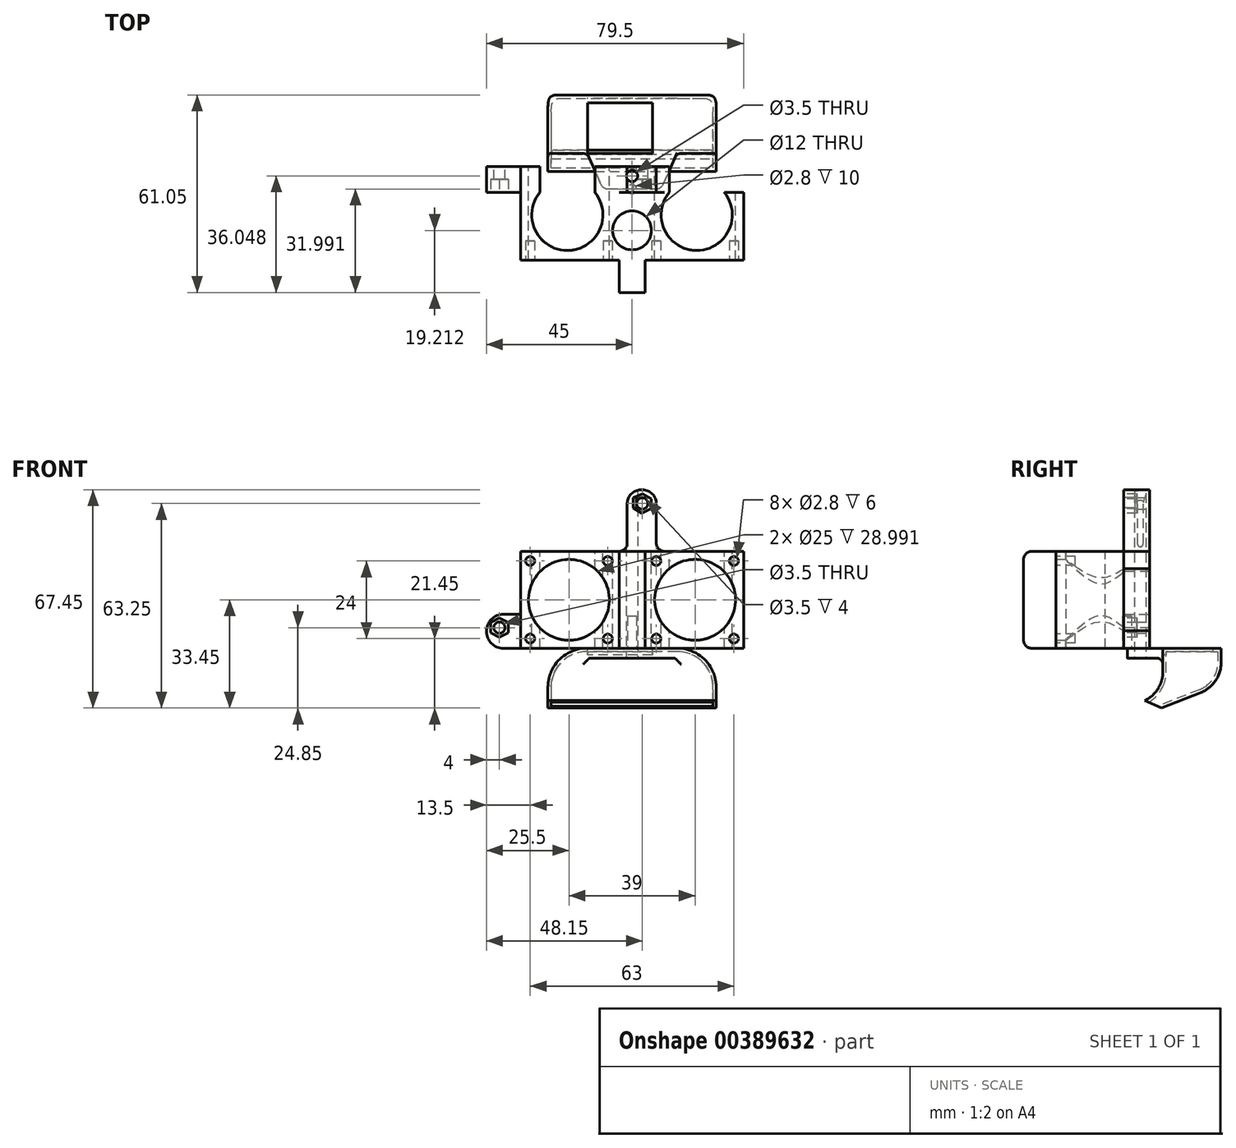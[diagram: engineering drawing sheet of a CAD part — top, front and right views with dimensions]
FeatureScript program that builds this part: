
annotation { "Feature Type Name" : "Feature", "Feature Type Description" : "" }
export const myFeature = defineFeature(function(context is Context, id is Id, definition is map)
    precondition{}
    {
        {
            var Q0;
            Q0=qCreatedBy(makeId("Front.planeOp"),FACE);
            var sketch = newSketch(context, id + "F0", { "sketchPlane" : qUnion([Q0])});
            skLineSegment(sketch, "E0.bottom", {"start": v(-34.5, 15) * mm, "end": v(-4.5, 15) * mm});
            skLineSegment(sketch, "E0.top", {"start": v(-34.5, -15) * mm, "end": v(-4.5, -15) * mm});
            skLineSegment(sketch, "E0.left", {"start": v(-34.5, 15) * mm, "end": v(-34.5, -15) * mm});
            skLineSegment(sketch, "E0.right", {"start": v(-4.5, 15) * mm, "end": v(-4.5, -15) * mm});
            skLineSegment(sketch, "E1.bottom", {"start": v(-31.5, 12) * mm, "end": v(-7.5, 12) * mm, "construction": true});
            skLineSegment(sketch, "E1.top", {"start": v(-31.5, -12) * mm, "end": v(-7.5, -12) * mm, "construction": true});
            skLineSegment(sketch, "E1.left", {"start": v(-31.5, 12) * mm, "end": v(-31.5, -12) * mm, "construction": true});
            skLineSegment(sketch, "E1.right", {"start": v(-7.5, 12) * mm, "end": v(-7.5, -12) * mm, "construction": true});
            skCircle(sketch, "E2", {"center": v(-31.5, 12) * mm, "radius": 1.4 * mm, "construction": true});
            skCircle(sketch, "E3", {"center": v(-7.5, 12) * mm, "radius": 1.4 * mm, "construction": true});
            skCircle(sketch, "E4", {"center": v(-7.5, -12) * mm, "radius": 1.4 * mm, "construction": true});
            skCircle(sketch, "E5", {"center": v(-31.5, -12) * mm, "radius": 1.4 * mm, "construction": true});
            skPoint(sketch, "E6", {"position": v(-19.5, 0) * mm});
            skPoint(sketch, "E6.positionSnap0", {"position": v(-7.5, 0) * mm});
            skPoint(sketch, "E6.positionSnap1", {"position": v(-19.5, -12) * mm});
            skCircle(sketch, "E7", {"center": v(-19.5, 0) * mm, "radius": 12.5 * mm});
            skLineSegment(sketch, "E8.bottom", {"start": v(-4.5, 15) * mm, "end": v(0, 15) * mm});
            skLineSegment(sketch, "E8.top", {"start": v(-4.5, -15) * mm, "end": v(0, -15) * mm});
            skLineSegment(sketch, "E8.right", {"start": v(0, 15) * mm, "end": v(0, -15) * mm});
            skSolve(sketch);
        }
        {
            var Q0;
            Q0=qSketchRegion(id+"F0",true);
            extrude(context, id + "F1", {"entities" : qUnion([Q0]), "depth" : 28 * mm});
        }
        {
            var Q0;
            Q0=makeQuery(id+"F1.opExtrude","SWEPT_FACE",FACE,{"disambiguationData":[OSD([sQuery(id+"F0.wireOp",EDGE,"E0.bottom")])]});
            var sketch = newSketch(context, id + "F2", { "sketchPlane" : qUnion([Q0])});
            skPoint(sketch, "E9.positionSnap0", {"position": v(-20, -28) * mm});
            skPoint(sketch, "E9.positionSnap1", {"position": v(-34.5, -14) * mm});
            skCircle(sketch, "E10", {"center": v(-20, -14) * mm, "radius": 11 * mm});
            skSolve(sketch);
        }
        {
            var Q0;
            Q0=qSketchRegion(id+"F2",true);
            extrude(context, id + "F3", {"entities" : qUnion([Q0]), "operationType" : NewBodyOperationType.REMOVE, "endBound" : BoundingType.THROUGH_ALL, "oppositeDirection" : true, "depth" : 25 * mm});
        }
        {
            var Q0;
            Q0=makeQuery(id+"F1.opExtrude","SWEPT_FACE",FACE,{"disambiguationData":[OSD([sQuery(id+"F0.wireOp",EDGE,"E0.bottom")])]});
            var sketch = newSketch(context, id + "F4", { "sketchPlane" : qUnion([Q0])});
            skLineSegment(sketch, "E11.bottom", {"start": v(-34.5, 0) * mm, "end": v(0, 0) * mm});
            skLineSegment(sketch, "E11.top", {"start": v(-34.5, -7) * mm, "end": v(0, -7) * mm});
            skLineSegment(sketch, "E11.left", {"start": v(-34.5, 0) * mm, "end": v(-34.5, -7) * mm});
            skLineSegment(sketch, "E11.right", {"start": v(0, 0) * mm, "end": v(0, -7) * mm});
            skSolve(sketch);
        }
        {
            var Q0;
            Q0=qSketchRegion(id+"F4",true);
            extrude(context, id + "F5", {"entities" : qUnion([Q0]), "operationType" : NewBodyOperationType.REMOVE, "endBound" : BoundingType.THROUGH_ALL, "oppositeDirection" : true, "depth" : 25 * mm});
        }
        {
            var Q0;
            Q0=makeQuery(id+"F1.opExtrude","CAP_FACE",FACE,{"disambiguationData":[OSD([sQuery(id+"F0.wireOp",EDGE,"E0.bottom"),sQuery(id+"F0.wireOp",EDGE,"E0.top"),sQuery(id+"F0.wireOp",EDGE,"E0.left"),sQuery(id+"F0.wireOp",EDGE,"E0.right"),sQuery(id+"F0.wireOp",EDGE,"E7")])],"isStart":false});
            var sketch = newSketch(context, id + "F6", { "sketchPlane" : qUnion([Q0])});
            skCircle(sketch, "E12.0", {"center": v(-31.5, 12) * mm, "radius": 1.4 * mm});
            skCircle(sketch, "E13.0", {"center": v(-7.5, 12) * mm, "radius": 1.4 * mm});
            skCircle(sketch, "E14.0", {"center": v(-7.5, -12) * mm, "radius": 1.4 * mm});
            skCircle(sketch, "E15.0", {"center": v(-31.5, -12) * mm, "radius": 1.4 * mm});
            skSolve(sketch);
        }
        {
            var Q0;
            Q0=qSketchRegion(id+"F6",true);
            extrude(context, id + "F7", {"entities" : qUnion([Q0]), "operationType" : NewBodyOperationType.REMOVE, "oppositeDirection" : true, "depth" : 6 * mm});
        }
        {
            var Q0;
            Q0=makeQuery(id+"F1.opExtrude","SWEPT_BODY",BODY,{"disambiguationData":[OSD([sQuery(id+"F0.wireOp",EDGE,"E0.bottom"),sQuery(id+"F0.wireOp",EDGE,"E0.top"),sQuery(id+"F0.wireOp",EDGE,"E0.left"),sQuery(id+"F0.wireOp",EDGE,"E0.right"),sQuery(id+"F0.wireOp",EDGE,"E7")])]});
            var Q1;
            Q1=qCreatedBy(makeId("Right.planeOp"),FACE);
            mirror(context, id + "F8", {"entities" : qUnion([Q0]), "mirrorPlane" : qUnion([Q1])});
        }
        {
            var Q0;
            Q0=makeQuery(id+"F1.opExtrude","SWEPT_BODY",BODY,{"disambiguationData":[OSD([sQuery(id+"F0.wireOp",EDGE,"E0.bottom"),sQuery(id+"F0.wireOp",EDGE,"E0.top"),sQuery(id+"F0.wireOp",EDGE,"E0.left"),sQuery(id+"F0.wireOp",EDGE,"E7"),sQuery(id+"F0.wireOp",EDGE,"E8.bottom"),sQuery(id+"F0.wireOp",EDGE,"E8.top"),sQuery(id+"F0.wireOp",EDGE,"E8.right")])]});
            var Q1;
            Q1=makeQuery(id+"F8.opPattern","COPY",BODY,{"derivedFrom":makeQuery(id+"F1.opExtrude","SWEPT_BODY",BODY,{"disambiguationData":[OSD([sQuery(id+"F0.wireOp",EDGE,"E0.bottom"),sQuery(id+"F0.wireOp",EDGE,"E0.top"),sQuery(id+"F0.wireOp",EDGE,"E0.left"),sQuery(id+"F0.wireOp",EDGE,"E7"),sQuery(id+"F0.wireOp",EDGE,"E8.bottom"),sQuery(id+"F0.wireOp",EDGE,"E8.top"),sQuery(id+"F0.wireOp",EDGE,"E8.right")])]}),"instanceName":"1"});
            booleanBodies(context, id + "F9", {"operationType" : BooleanOperationType.UNION, "tools" : qUnion([Q0, Q1])});
        }
        {
            var Q0;
            {var subQ0=makeQuery(id+"F5.boolean.opBoolean","COPY",FACE,{"disambiguationData":[TD([makeQuery(id+"F1.opExtrude","SWEPT_FACE",FACE,{"disambiguationData":[OSD([sQuery(id+"F0.wireOp",EDGE,"E8.right")])]})])],"derivedFrom":makeQuery(id+"F5.opExtrude","SWEPT_FACE",FACE,{"disambiguationData":[OSD([sQuery(id+"F4.wireOp",EDGE,"E11.top")])]})});Q0=makeQuery(id+"F9.opBoolean","MERGE",FACE,{"derivedFrom":[subQ0,makeQuery(id+"F8.opPattern","COPY",FACE,{"derivedFrom":subQ0,"instanceName":"1"})]});}
            var sketch = newSketch(context, id + "F10", { "sketchPlane" : qUnion([Q0])});
            skLineSegment(sketch, "E16.bottom", {"start": v(-7.5, 15) * mm, "end": v(1.5, 15) * mm});
            skLineSegment(sketch, "E16.top", {"start": v(-7.5, 34) * mm, "end": v(1.5, 34) * mm});
            skLineSegment(sketch, "E16.left", {"start": v(-7.5, 15) * mm, "end": v(-7.5, 34) * mm});
            skLineSegment(sketch, "E16.right", {"start": v(1.5, 15) * mm, "end": v(1.5, 34) * mm});
            skPoint(sketch, "E17.orphan", {"position": v(0, 34) * mm});
            skLineSegment(sketch, "E18.0.0", {"start": v(11.5, -9.61) * mm, "end": v(11.5, -15) * mm});
            skArc(sketch, "E18.0.1", {"start": v(11.5, -9.61) * mm, "mid": v(7, 0) * mm, "end": v(11.5, 9.61) * mm});
            skLineSegment(sketch, "E18.0.2", {"start": v(11.5, 15) * mm, "end": v(11.5, 9.61) * mm});
            skLineSegment(sketch, "E18.0.3", {"start": v(11.5, 15) * mm, "end": v(-11.5, 15) * mm});
            skLineSegment(sketch, "E18.0.4", {"start": v(-11.5, 15) * mm, "end": v(-11.5, 9.61) * mm});
            skArc(sketch, "E18.0.5", {"start": v(-11.5, 9.61) * mm, "mid": v(-7, 0) * mm, "end": v(-11.5, -9.61) * mm});
            skLineSegment(sketch, "E18.0.6", {"start": v(-11.5, -9.61) * mm, "end": v(-11.5, -15) * mm});
            skLineSegment(sketch, "E18.0.7", {"start": v(-11.5, -15) * mm, "end": v(11.5, -15) * mm});
            skLineSegment(sketch, "E19.0.0", {"start": v(34.5, -15) * mm, "end": v(34.5, 15) * mm});
            skLineSegment(sketch, "E19.0.1", {"start": v(34.5, 15) * mm, "end": v(28.5, 15) * mm});
            skLineSegment(sketch, "E19.0.2", {"start": v(28.5, 15) * mm, "end": v(28.5, 8.68) * mm});
            skArc(sketch, "E19.0.3", {"start": v(28.5, 8.68) * mm, "mid": v(32, 0) * mm, "end": v(28.5, -8.68) * mm});
            skLineSegment(sketch, "E19.0.4", {"start": v(28.5, -8.68) * mm, "end": v(28.5, -15) * mm});
            skLineSegment(sketch, "E19.0.5", {"start": v(28.5, -15) * mm, "end": v(34.5, -15) * mm});
            skSolve(sketch);
        }
        {
            var Q0;
            Q0=qSketchRegion(id+"F10",true);
            extrude(context, id + "F11", {"entities" : qUnion([Q0]), "operationType" : NewBodyOperationType.ADD, "depth" : 8 * mm});
        }
        {
            var Q0;
            Q0=makeQuery(id+"F11.opExtrude","SWEPT_EDGE",EDGE,{"disambiguationData":[OSD([sQuery(id+"F10.wireOp",EDGE,"E16.top"),sQuery(id+"F10.wireOp",EDGE,"E16.right")])]});
            var Q1;
            Q1=makeQuery(id+"F11.opExtrude","SWEPT_EDGE",EDGE,{"disambiguationData":[OSD([sQuery(id+"F10.wireOp",EDGE,"E16.top"),sQuery(id+"F10.wireOp",EDGE,"E16.left")])]});
            fillet(context, id + "F12", {"entities" : qUnion([Q0, Q1]), "radius" : 4.25 * mm, "tangentPropagation" : true, "allowEdgeOverflow" : false});
        }
        {
            var Q0;
            Q0=makeQuery(id+"F11.opExtrude","CAP_FACE",FACE,{"disambiguationData":[OSD([sQuery(id+"F10.wireOp",EDGE,"E19.0.0"),sQuery(id+"F10.wireOp",EDGE,"E19.0.1"),sQuery(id+"F10.wireOp",EDGE,"E19.0.2"),sQuery(id+"F10.wireOp",EDGE,"E19.0.3"),sQuery(id+"F10.wireOp",EDGE,"E19.0.4"),sQuery(id+"F10.wireOp",EDGE,"E19.0.5")])],"isStart":false});
            var sketch = newSketch(context, id + "F13", { "sketchPlane" : qUnion([Q0])});
            skLineSegment(sketch, "E20.bottom", {"start": v(34.5, -4.5) * mm, "end": v(45, -4.5) * mm});
            skLineSegment(sketch, "E20.top", {"start": v(34.5, -15) * mm, "end": v(45, -15) * mm});
            skLineSegment(sketch, "E20.left", {"start": v(34.5, -4.5) * mm, "end": v(34.5, -15) * mm});
            skLineSegment(sketch, "E20.right", {"start": v(45, -4.5) * mm, "end": v(45, -15) * mm});
            skSolve(sketch);
        }
        {
            var Q0;
            Q0=qSketchRegion(id+"F13",true);
            extrude(context, id + "F14", {"entities" : qUnion([Q0]), "operationType" : NewBodyOperationType.ADD, "oppositeDirection" : true, "depth" : 8 * mm});
        }
        {
            var Q0;
            Q0=makeQuery(id+"F14.boolean.opBoolean","MERGE",FACE,{"derivedFrom":[makeQuery(id+"F11.opExtrude","CAP_FACE",FACE,{"disambiguationData":[OSD([sQuery(id+"F10.wireOp",EDGE,"d3302207-0b7b-4ae5-a757-db3abba19617.0.0"),sQuery(id+"F10.wireOp",EDGE,"d3302207-0b7b-4ae5-a757-db3abba19617.0.1"),sQuery(id+"F10.wireOp",EDGE,"d3302207-0b7b-4ae5-a757-db3abba19617.0.2"),sQuery(id+"F10.wireOp",EDGE,"d3302207-0b7b-4ae5-a757-db3abba19617.0.3"),sQuery(id+"F10.wireOp",EDGE,"d3302207-0b7b-4ae5-a757-db3abba19617.0.4"),sQuery(id+"F10.wireOp",EDGE,"d3302207-0b7b-4ae5-a757-db3abba19617.0.5")])],"isStart":false}),makeQuery(id+"F14.opExtrude","CAP_FACE",FACE,{"disambiguationData":[OSD([sQuery(id+"F13.wireOp",EDGE,"E20.bottom"),sQuery(id+"F13.wireOp",EDGE,"E20.top"),sQuery(id+"F13.wireOp",EDGE,"E20.left"),sQuery(id+"F13.wireOp",EDGE,"E20.right")])],"isStart":true})]});
            var sketch = newSketch(context, id + "F15", { "sketchPlane" : qUnion([Q0])});
            skCircle(sketch, "E21", {"center": v(41, -8.6) * mm, "radius": 1.75 * mm});
            skCircle(sketch, "E22", {"center": v(-3.15, 29.8) * mm, "radius": 1.75 * mm});
            skSolve(sketch);
        }
        {
            var Q0;
            Q0=qSketchRegion(id+"F15",true);
            extrude(context, id + "F16", {"entities" : qUnion([Q0]), "operationType" : NewBodyOperationType.REMOVE, "endBound" : BoundingType.THROUGH_ALL, "oppositeDirection" : true, "depth" : 25 * mm});
        }
        {
            var Q0;
            {var subQ0=sQuery(id+"F10.wireOp",EDGE,"67f7da67-8d9d-40b1-a9e6-b95f429b4137.0.0");var subQ1=makeQuery(id+"F1.opExtrude","SWEPT_FACE",FACE,{"disambiguationData":[OSD([sQuery(id+"F0.wireOp",EDGE,"E0.bottom"),sQuery(id+"F0.wireOp",EDGE,"E8.bottom")])]});var subQ3=sQuery(id+"F10.wireOp",EDGE,"E16.bottom");var subQ4=subQ1;Q0=makeQuery(id+"F11.boolean.opBoolean","MERGE",FACE,{"derivedFrom":[makeQuery(id+"F9.opBoolean","MERGE",FACE,{"derivedFrom":[subQ4,makeQuery(id+"F8.opPattern","COPY",FACE,{"derivedFrom":subQ4,"instanceName":"1"})]}),makeQuery(id+"F11.opExtrude","SWEPT_FACE",FACE,{"disambiguationData":[OSD([subQ0]),TDD([makeQuery(id+"F10.imprint","IMPRINT",EDGE,{"disambiguationData":[TD([[makeQuery(id+"F10.imprint","INTERSECT",VERTEX,{"derivedFrom":[subQ0,subQ3,sQuery(id+"F10.wireOp",EDGE,"E16.right")]}),1.0]])],"derivedFrom":subQ0})])]}),makeQuery(id+"F11.opExtrude","SWEPT_FACE",FACE,{"disambiguationData":[OSD([subQ0]),TDD([makeQuery(id+"F10.imprint","IMPRINT",EDGE,{"disambiguationData":[TD([[makeQuery(id+"F10.imprint","INTERSECT",VERTEX,{"derivedFrom":[subQ0,subQ3,sQuery(id+"F10.wireOp",EDGE,"E16.left")]}),-1.0]])],"derivedFrom":subQ0})])]}),makeQuery(id+"F11.opExtrude","SWEPT_FACE",FACE,{"disambiguationData":[OSD([sQuery(id+"F10.wireOp",EDGE,"d3302207-0b7b-4ae5-a757-db3abba19617.0.1")])]})]});}
            var sketch = newSketch(context, id + "F17", { "sketchPlane" : qUnion([Q0])});
            skCircle(sketch, "E23", {"center": v(0, -18.79) * mm, "radius": 6 * mm});
            skSolve(sketch);
        }
        {
            var Q0;
            Q0=qSketchRegion(id+"F17",true);
            extrude(context, id + "F18", {"entities" : qUnion([Q0]), "operationType" : NewBodyOperationType.REMOVE, "endBound" : BoundingType.THROUGH_ALL, "oppositeDirection" : true, "depth" : 25 * mm});
        }
        {
            var Q0;
            {var subQ0=makeQuery(id+"F1.opExtrude","CAP_FACE",FACE,{"disambiguationData":[OSD([sQuery(id+"F0.wireOp",EDGE,"E0.bottom"),sQuery(id+"F0.wireOp",EDGE,"E0.top"),sQuery(id+"F0.wireOp",EDGE,"E0.left"),sQuery(id+"F0.wireOp",EDGE,"E7"),sQuery(id+"F0.wireOp",EDGE,"E8.bottom"),sQuery(id+"F0.wireOp",EDGE,"E8.top"),sQuery(id+"F0.wireOp",EDGE,"E8.right")])],"isStart":false});Q0=makeQuery(id+"F9.opBoolean","MERGE",FACE,{"derivedFrom":[subQ0,makeQuery(id+"F8.opPattern","COPY",FACE,{"derivedFrom":subQ0,"instanceName":"1"})]});}
            var sketch = newSketch(context, id + "F19", { "sketchPlane" : qUnion([Q0])});
            skLineSegment(sketch, "E24.bottom", {"start": v(0, -15) * mm, "end": v(4, -15) * mm});
            skLineSegment(sketch, "E24.top", {"start": v(0, 15) * mm, "end": v(4, 15) * mm});
            skLineSegment(sketch, "E24.left", {"start": v(0, -15) * mm, "end": v(0, 15) * mm});
            skLineSegment(sketch, "E24.right", {"start": v(4, -15) * mm, "end": v(4, 15) * mm});
            skLineSegment(sketch, "E25.MirrorCS", {"start": v(0, 15) * mm, "end": v(-4, 15) * mm});
            skLineSegment(sketch, "E26.MirrorCS", {"start": v(-4, -15) * mm, "end": v(-4, 15) * mm});
            skLineSegment(sketch, "E27.MirrorCS", {"start": v(0, -15) * mm, "end": v(-4, -15) * mm});
            skSolve(sketch);
        }
        {
            var Q0;
            Q0=qSketchRegion(id+"F19",true);
            extrude(context, id + "F20", {"entities" : qUnion([Q0]), "operationType" : NewBodyOperationType.ADD, "depth" : 10 * mm});
        }
        {
            var Q0;
            Q0=makeQuery(id+"F14.opExtrude","SWEPT_EDGE",EDGE,{"disambiguationData":[OSD([sQuery(id+"F13.wireOp",EDGE,"E20.bottom"),sQuery(id+"F13.wireOp",EDGE,"E20.right")])]});
            var Q1;
            Q1=makeQuery(id+"F14.opExtrude","SWEPT_EDGE",EDGE,{"disambiguationData":[OSD([sQuery(id+"F13.wireOp",EDGE,"E20.top"),sQuery(id+"F13.wireOp",EDGE,"E20.right")])]});
            fillet(context, id + "F21", {"entities" : qUnion([Q0, Q1]), "radius" : 5.25 * mm, "tangentPropagation" : true, "allowEdgeOverflow" : false});
        }
        {
            var Q0;
            Q0=makeQuery(id+"F14.opExtrude","SWEPT_EDGE",EDGE,{"disambiguationData":[OSD([sQuery(id+"F10.wireOp",EDGE,"d3302207-0b7b-4ae5-a757-db3abba19617.0.0"),sQuery(id+"F13.wireOp",EDGE,"E20.bottom"),sQuery(id+"F13.wireOp",EDGE,"E20.left")])]});
            var Q1;
            Q1=makeQuery(id+"F11.opExtrude","SWEPT_EDGE",EDGE,{"disambiguationData":[OSD([sQuery(id+"F10.wireOp",EDGE,"67f7da67-8d9d-40b1-a9e6-b95f429b4137.0.0"),sQuery(id+"F10.wireOp",EDGE,"E16.bottom"),sQuery(id+"F10.wireOp",EDGE,"E16.right")])]});
            var Q2;
            Q2=makeQuery(id+"F11.opExtrude","SWEPT_EDGE",EDGE,{"disambiguationData":[OSD([sQuery(id+"F10.wireOp",EDGE,"67f7da67-8d9d-40b1-a9e6-b95f429b4137.0.0"),sQuery(id+"F10.wireOp",EDGE,"E16.bottom"),sQuery(id+"F10.wireOp",EDGE,"E16.left")])]});
            fillet(context, id + "F22", {"entities" : qUnion([Q0, Q1, Q2]), "radius" : 2.5 * mm, "tangentPropagation" : true, "allowEdgeOverflow" : false});
        }
        {
            var Q0;
            Q0=makeQuery(id+"F20.opExtrude","CAP_EDGE",EDGE,{"disambiguationData":[OSD([sQuery(id+"F19.wireOp",EDGE,"E24.top"),sQuery(id+"F19.wireOp",EDGE,"E25.MirrorCS")])],"isStart":false});
            var Q1;
            Q1=makeQuery(id+"F20.opExtrude","CAP_EDGE",EDGE,{"disambiguationData":[OSD([sQuery(id+"F19.wireOp",EDGE,"E24.bottom"),sQuery(id+"F19.wireOp",EDGE,"E27.MirrorCS")])],"isStart":false});
            fillet(context, id + "F23", {"entities" : qUnion([Q0, Q1]), "radius" : 2.5 * mm, "tangentPropagation" : true, "allowEdgeOverflow" : false});
        }
        {
            var Q0;
            {var subQ0=makeQuery(id+"F1.opExtrude","SWEPT_FACE",FACE,{"disambiguationData":[OSD([sQuery(id+"F0.wireOp",EDGE,"E0.top"),sQuery(id+"F0.wireOp",EDGE,"E8.top")])]});Q0=makeQuery(id+"F20.boolean.opBoolean","MERGE",FACE,{"derivedFrom":[makeQuery(id+"F14.boolean.opBoolean","MERGE",FACE,{"derivedFrom":[makeQuery(id+"F11.boolean.opBoolean","MERGE",FACE,{"derivedFrom":[makeQuery(id+"F9.opBoolean","MERGE",FACE,{"derivedFrom":[subQ0,makeQuery(id+"F8.opPattern","COPY",FACE,{"derivedFrom":subQ0,"instanceName":"1"})]}),makeQuery(id+"F11.opExtrude","SWEPT_FACE",FACE,{"disambiguationData":[OSD([sQuery(id+"F10.wireOp",EDGE,"E18.0.7")])]}),makeQuery(id+"F11.opExtrude","SWEPT_FACE",FACE,{"disambiguationData":[OSD([sQuery(id+"F10.wireOp",EDGE,"E19.0.5")])]})]}),makeQuery(id+"F14.opExtrude","SWEPT_FACE",FACE,{"disambiguationData":[OSD([sQuery(id+"F13.wireOp",EDGE,"E20.top")])]})]}),makeQuery(id+"F20.opExtrude","SWEPT_FACE",FACE,{"disambiguationData":[OSD([sQuery(id+"F19.wireOp",EDGE,"E24.bottom"),sQuery(id+"F19.wireOp",EDGE,"E27.MirrorCS")])]})]});}
            var sketch = newSketch(context, id + "F24", { "sketchPlane" : qUnion([Q0])});
            skCircle(sketch, "E28", {"center": v(0, 6) * mm, "radius": 1.4 * mm});
            skSolve(sketch);
        }
        {
            var Q0;
            Q0=makeQuery(id+"F24.imprint","IMPRINT",FACE,{"disambiguationData":[TD([[makeQuery(id+"F24.imprint","IMPRINT",EDGE,{"derivedFrom":sQuery(id+"F24.wireOp",EDGE,"E28")}),1.0]])]});
            extrude(context, id + "F25", {"entities" : qUnion([Q0]), "operationType" : NewBodyOperationType.REMOVE, "oppositeDirection" : true, "depth" : 10 * mm});
        }
        {
            var Q0;
            Q0=qCreatedBy(makeId("Top.planeOp"),FACE);
            cPlane(context, id + "F26", {"entities" : qUnion([Q0]), "cplaneType" : CPlaneType.OFFSET, "offset" : 15 * mm, "oppositeDirection" : true, "width" : 150 * mm, "height" : 150 * mm});
        }
        {
            var Q0;
            Q0=qCreatedBy(makeId("Right.planeOp"),FACE);
            cPlane(context, id + "F27", {"entities" : qUnion([Q0]), "cplaneType" : CPlaneType.OFFSET, "offset" : 0 * mm, "width" : 150 * mm, "height" : 150 * mm});
        }
        {
            var Q0;
            Q0=qCreatedBy(id+"F27.planeOp",FACE);
            var sketch = newSketch(context, id + "F28", { "sketchPlane" : qUnion([Q0])});
            skLineSegment(sketch, "E29", {"start": v(5.05, -15) * mm, "end": v(23.05, -15) * mm});
            skLineSegment(sketch, "E30", {"start": v(23.05, -15) * mm, "end": v(23.05, -18) * mm});
            skLineSegment(sketch, "E31", {"start": v(23.05, -18) * mm, "end": v(23.05, -26.21) * mm});
            skLineSegment(sketch, "E32", {"start": v(23.05, -26.21) * mm, "end": v(0, -35.29) * mm});
            skLineSegment(sketch, "E33", {"start": v(0, -35.29) * mm, "end": v(-1.47, -31.56) * mm});
            skLineSegment(sketch, "E34", {"start": v(-1.47, -31.56) * mm, "end": v(5.05, -29) * mm});
            skLineSegment(sketch, "E35", {"start": v(5.05, -29) * mm, "end": v(5.05, -15) * mm});
            skSolve(sketch);
        }
        {
            var Q0;
            Q0=qSketchRegion(id+"F28",true);
            extrude(context, id + "F29", {"entities" : qUnion([Q0]), "depth" : 26 * mm});
        }
        {
            var Q0;
            {var subQ0=makeQuery(id+"F29.opExtrude","SWEPT_EDGE",EDGE,{"disambiguationData":[OSD([sQuery(id+"F28.wireOp",EDGE,"E31"),sQuery(id+"F28.wireOp",EDGE,"E32")])]});Q0=makeQuery(id+"FV71bhgb1KHxjhJ_2.boolean.opBoolean","MERGE",EDGE,{"derivedFrom":[subQ0,makeQuery(id+"FV71bhgb1KHxjhJ_2.opPattern","COPY",EDGE,{"derivedFrom":subQ0,"instanceName":"1"})]});}
            var Q1;
            {var subQ0=makeQuery(id+"F29.opExtrude","SWEPT_EDGE",EDGE,{"disambiguationData":[OSD([sQuery(id+"F28.wireOp",EDGE,"E34"),sQuery(id+"F28.wireOp",EDGE,"E35")])]});Q1=makeQuery(id+"FV71bhgb1KHxjhJ_2.boolean.opBoolean","MERGE",EDGE,{"derivedFrom":[subQ0,makeQuery(id+"FV71bhgb1KHxjhJ_2.opPattern","COPY",EDGE,{"derivedFrom":subQ0,"instanceName":"1"})]});}
            fillet(context, id + "F30", {"entities" : qUnion([Q0, Q1]), "radius" : 10 * mm, "tangentPropagation" : true, "allowEdgeOverflow" : false});
        }
        {
            var Q0;
            Q0=makeQuery(id+"F29.opExtrude","CAP_FACE",FACE,{"disambiguationData":[OSD([sQuery(id+"F28.wireOp",EDGE,"E29"),sQuery(id+"F28.wireOp",EDGE,"E30"),sQuery(id+"F28.wireOp",EDGE,"E31"),sQuery(id+"F28.wireOp",EDGE,"E32"),sQuery(id+"F28.wireOp",EDGE,"E33"),sQuery(id+"F28.wireOp",EDGE,"E34"),sQuery(id+"F28.wireOp",EDGE,"E35")])],"isStart":true});
            var sketch = newSketch(context, id + "F31", { "sketchPlane" : qUnion([Q0])});
            skLineSegment(sketch, "E36.0.0", {"start": v(-23.05, -15) * mm, "end": v(-23.05, -19.4) * mm});
            skArc(sketch, "E36.0.1", {"start": v(-23.05, -19.4) * mm, "mid": v(-21.31, -25.03) * mm, "end": v(-16.71, -28.7) * mm});
            skLineSegment(sketch, "E36.0.2", {"start": v(-16.71, -28.7) * mm, "end": v(0, -35.29) * mm});
            skLineSegment(sketch, "E36.0.3", {"start": v(0, -35.29) * mm, "end": v(1.47, -31.56) * mm});
            skArc(sketch, "E36.0.4", {"start": v(1.47, -31.56) * mm, "mid": v(-3.26, -27.9) * mm, "end": v(-5.05, -22.19) * mm});
            skLineSegment(sketch, "E36.0.5", {"start": v(-5.05, -22.19) * mm, "end": v(-5.05, -15) * mm});
            skLineSegment(sketch, "E36.0.6", {"start": v(-5.05, -15) * mm, "end": v(-23.05, -15) * mm});
            skSolve(sketch);
        }
        {
            var Q0;
            Q0=qSketchRegion(id+"F31",true);
            extrude(context, id + "F32", {"entities" : qUnion([Q0]), "operationType" : NewBodyOperationType.ADD, "depth" : 26 * mm});
        }
        {
            var Q0;
            Q0=makeQuery(id+"F32.boolean.opBoolean","MERGE",EDGE,{"derivedFrom":[makeQuery(id+"F29.opExtrude","SWEPT_EDGE",EDGE,{"disambiguationData":[OSD([sQuery(id+"F28.wireOp",EDGE,"E32"),sQuery(id+"F28.wireOp",EDGE,"E33")])]}),makeQuery(id+"F32.opExtrude","SWEPT_EDGE",EDGE,{"disambiguationData":[OSD([sQuery(id+"F31.wireOp",EDGE,"E36.0.2"),sQuery(id+"F31.wireOp",EDGE,"E36.0.3")])]})]});
            chamfer(context, id + "F33", {"entities" : qUnion([Q0]), "width" : 5 * mm, "tangentPropagation" : true});
        }
        {
            var Q0;
            Q0=makeQuery(id+"F29.opExtrude","CAP_EDGE",EDGE,{"disambiguationData":[OSD([sQuery(id+"F28.wireOp",EDGE,"E29")])],"isStart":false});
            var Q1;
            Q1=makeQuery(id+"F32.opExtrude","CAP_EDGE",EDGE,{"disambiguationData":[OSD([sQuery(id+"F31.wireOp",EDGE,"E36.0.6")])],"isStart":false});
            fillet(context, id + "F34", {"entities" : qUnion([Q0, Q1]), "radius" : 12 * mm, "tangentPropagation" : true, "allowEdgeOverflow" : false});
        }
        {
            var Q0;
            Q0=makeQuery(id+"F33.opChamfer","BLEND_FACE",FACE,{"disambiguationData":[OSD([sQuery(id+"F28.wireOp",EDGE,"E32"),sQuery(id+"F28.wireOp",EDGE,"E33"),sQuery(id+"F31.wireOp",EDGE,"E36.0.2"),sQuery(id+"F31.wireOp",EDGE,"E36.0.3")])]});
            shell(context, id + "F35", {"entities" : qUnion([Q0]), "thickness" : 1 * mm});
        }
        {
            var Q0;
            Q0=makeQuery(id+"F32.boolean.opBoolean","MERGE",FACE,{"derivedFrom":[makeQuery(id+"F29.opExtrude","SWEPT_FACE",FACE,{"disambiguationData":[OSD([sQuery(id+"F28.wireOp",EDGE,"E29")])]}),makeQuery(id+"F32.opExtrude","SWEPT_FACE",FACE,{"disambiguationData":[OSD([sQuery(id+"F31.wireOp",EDGE,"E36.0.6")])]})]});
            var sketch = newSketch(context, id + "F36", { "sketchPlane" : qUnion([Q0])});
            skLineSegment(sketch, "E37.bottom", {"start": v(-13.8, 20.62) * mm, "end": v(6.32, 20.62) * mm});
            skLineSegment(sketch, "E37.top", {"start": v(-13.8, 5.05) * mm, "end": v(6.32, 5.05) * mm});
            skLineSegment(sketch, "E37.left", {"start": v(-13.8, 20.62) * mm, "end": v(-13.8, 5.05) * mm});
            skLineSegment(sketch, "E37.right", {"start": v(6.32, 20.62) * mm, "end": v(6.32, 5.05) * mm});
            skSolve(sketch);
        }
        {
            var Q0;
            Q0=qSketchRegion(id+"F36",true);
            extrude(context, id + "F37", {"entities" : qUnion([Q0]), "operationType" : NewBodyOperationType.REMOVE, "oppositeDirection" : true, "depth" : 2 * mm});
        }
        {
            var Q0;
            Q0=makeQuery(id+"F32.boolean.opBoolean","MERGE",FACE,{"derivedFrom":[makeQuery(id+"F29.opExtrude","SWEPT_FACE",FACE,{"disambiguationData":[OSD([sQuery(id+"F28.wireOp",EDGE,"E35")])]}),makeQuery(id+"F32.opExtrude","SWEPT_FACE",FACE,{"disambiguationData":[OSD([sQuery(id+"F31.wireOp",EDGE,"E36.0.5")])]})]});
            var sketch = newSketch(context, id + "F38", { "sketchPlane" : qUnion([Q0])});
            skLineSegment(sketch, "E38.bottom", {"start": v(-14, -22.19) * mm, "end": v(14, -22.19) * mm});
            skLineSegment(sketch, "E38.top", {"start": v(-14, -15) * mm, "end": v(14, -15) * mm});
            skLineSegment(sketch, "E38.left", {"start": v(-14, -22.19) * mm, "end": v(-14, -15) * mm});
            skLineSegment(sketch, "E38.right", {"start": v(14, -22.19) * mm, "end": v(14, -15) * mm});
            skSolve(sketch);
        }
        {
            var Q0;
            Q0=qSketchRegion(id+"F38",true);
            extrude(context, id + "F39", {"entities" : qUnion([Q0]), "operationType" : NewBodyOperationType.ADD, "depth" : 11 * mm});
        }
        {
            var Q0;
            Q0=makeQuery(id+"F39.opExtrude","SWEPT_FACE",FACE,{"disambiguationData":[OSD([sQuery(id+"F38.wireOp",EDGE,"E38.bottom")])]});
            var sketch = newSketch(context, id + "F40", { "sketchPlane" : qUnion([Q0])});
            skCircle(sketch, "E39", {"center": v(0, 1.95) * mm, "radius": 1.75 * mm});
            skSolve(sketch);
        }
        {
            var Q0;
            Q0=makeQuery(id+"F40.imprint","IMPRINT",FACE,{"disambiguationData":[TD([[makeQuery(id+"F40.imprint","IMPRINT",EDGE,{"derivedFrom":sQuery(id+"F40.wireOp",EDGE,"E39")}),1.0]])]});
            extrude(context, id + "F41", {"entities" : qUnion([Q0]), "operationType" : NewBodyOperationType.REMOVE, "endBound" : BoundingType.THROUGH_ALL, "oppositeDirection" : true, "depth" : 25 * mm});
        }
        {
            var Q0;
            Q0=makeQuery(id+"F4G2US6mc5SEyC5_2.boolean.opBoolean","MERGE",FACE,{"derivedFrom":[makeQuery(id+"F39.opExtrude","CAP_FACE",FACE,{"disambiguationData":[OSD([sQuery(id+"F38.wireOp",EDGE,"E38.bottom"),sQuery(id+"F38.wireOp",EDGE,"E38.top"),sQuery(id+"F38.wireOp",EDGE,"E38.left"),sQuery(id+"F38.wireOp",EDGE,"E38.right")])],"isStart":false}),makeQuery(id+"F4G2US6mc5SEyC5_2.opExtrude","SWEPT_FACE",FACE,{"disambiguationData":[OSD([sQuery(id+"Fvcmfcm8lbraAiA_2.wireOp",EDGE,"525e9192-7aa1-427e-b2e2-4a4418798a99.0.3")])]})]});
            var sketch = newSketch(context, id + "F42", { "sketchPlane" : qUnion([Q0])});
            skLineSegment(sketch, "E40.0.0", {"start": v(-14, -22.19) * mm, "end": v(14, -22.19) * mm});
            skPoint(sketch, "E40.0.3.end.orphan", {"position": v(-14, -15) * mm});
            skPoint(sketch, "E40.0.1.end.orphan", {"position": v(15.5, -15) * mm});
            skPoint(sketch, "E40.0.4.start.orphan", {"position": v(-14, -15) * mm});
            skLineSegment(sketch, "E41", {"start": v(-14, -22.19) * mm, "end": v(-14, -18) * mm});
            skLineSegment(sketch, "E42", {"start": v(-14, -18) * mm, "end": v(14, -18) * mm});
            skLineSegment(sketch, "E43", {"start": v(14, -22.19) * mm, "end": v(14, -18) * mm});
            skSolve(sketch);
        }
        {
            var Q0;
            Q0=qSketchRegion(id+"F42",true);
            var Q1;
            {var subQ0=sQuery(id+"F31.wireOp",EDGE,"E36.0.6");var subQ1=sQuery(id+"F28.wireOp",EDGE,"E35");Q1=makeQuery(id+"F39.boolean.opBoolean","SPLIT",FACE,{"disambiguationData":[TD([makeQuery(id+"F34.opFillet","BLEND_FACE",FACE,{"disambiguationData":[OSD([subQ0])]})])],"derivedFrom":makeQuery(id+"F32.boolean.opBoolean","MERGE",FACE,{"derivedFrom":[makeQuery(id+"F29.opExtrude","SWEPT_FACE",FACE,{"disambiguationData":[OSD([subQ1])]}),makeQuery(id+"F32.opExtrude","SWEPT_FACE",FACE,{"disambiguationData":[OSD([sQuery(id+"F31.wireOp",EDGE,"E36.0.5")])]})]})});}
            extrude(context, id + "F43", {"entities" : qUnion([Q0]), "operationType" : NewBodyOperationType.REMOVE, "endBound" : BoundingType.UP_TO_SURFACE, "oppositeDirection" : true, "endBoundEntityFace" : qUnion([Q1]), "depth" : 25 * mm});
        }
        {
            var Q0;
            Q0=makeQuery(id+"F39.opExtrude","CAP_EDGE",EDGE,{"disambiguationData":[OSD([sQuery(id+"F38.wireOp",EDGE,"E38.right")])],"isStart":false});
            var Q1;
            Q1=makeQuery(id+"F39.opExtrude","CAP_EDGE",EDGE,{"disambiguationData":[OSD([sQuery(id+"F38.wireOp",EDGE,"E38.left")])],"isStart":false});
            chamfer(context, id + "F44", {"entities" : qUnion([Q0, Q1]), "chamferType" : ChamferType.OFFSET_ANGLE, "width" : 5 * mm, "oppositeDirection" : false, "angle" : 66 * degree, "tangentPropagation" : true});
        }
        {
            var Q0;
            {var subQ0=sQuery(id+"F38.wireOp",EDGE,"E38.right");Q0=makeQuery(id+"F44.opChamfer","BLEND_EDGE",EDGE,{"blendedFrom":[makeQuery(id+"F39.opExtrude","CAP_EDGE",EDGE,{"disambiguationData":[OSD([subQ0])],"isStart":false}),makeQuery(id+"F39.opExtrude","CAP_FACE",FACE,{"disambiguationData":[OSD([sQuery(id+"F38.wireOp",EDGE,"E38.bottom"),sQuery(id+"F38.wireOp",EDGE,"E38.top"),sQuery(id+"F38.wireOp",EDGE,"E38.left"),subQ0])],"isStart":false})],"blendedInto":[makeQuery(id+"F39.opExtrude","CAP_FACE",FACE,{"disambiguationData":[OSD([sQuery(id+"F38.wireOp",EDGE,"E38.bottom"),sQuery(id+"F38.wireOp",EDGE,"E38.top"),sQuery(id+"F38.wireOp",EDGE,"E38.left"),subQ0])],"isStart":false})]});}
            var Q1;
            {var subQ0=sQuery(id+"F38.wireOp",EDGE,"E38.left");Q1=makeQuery(id+"F44.opChamfer","BLEND_EDGE",EDGE,{"blendedFrom":[makeQuery(id+"F39.opExtrude","CAP_EDGE",EDGE,{"disambiguationData":[OSD([subQ0])],"isStart":false}),makeQuery(id+"F39.opExtrude","CAP_FACE",FACE,{"disambiguationData":[OSD([sQuery(id+"F38.wireOp",EDGE,"E38.bottom"),sQuery(id+"F38.wireOp",EDGE,"E38.top"),subQ0,sQuery(id+"F38.wireOp",EDGE,"E38.right")])],"isStart":false})],"blendedInto":[makeQuery(id+"F39.opExtrude","CAP_FACE",FACE,{"disambiguationData":[OSD([sQuery(id+"F38.wireOp",EDGE,"E38.bottom"),sQuery(id+"F38.wireOp",EDGE,"E38.top"),subQ0,sQuery(id+"F38.wireOp",EDGE,"E38.right")])],"isStart":false})]});}
            fillet(context, id + "F45", {"entities" : qUnion([Q0, Q1]), "radius" : 2.5 * mm, "tangentPropagation" : true, "allowEdgeOverflow" : false});
        }
        {
            var Q0;
            {var subQ0=sQuery(id+"F31.wireOp",EDGE,"E36.0.6");var subQ3=sQuery(id+"F28.wireOp",EDGE,"E35");var subQ7=sQuery(id+"F28.wireOp",EDGE,"E29");var subQ9=makeQuery(id+"F32.boolean.opBoolean","MERGE",FACE,{"derivedFrom":[makeQuery(id+"F29.opExtrude","SWEPT_FACE",FACE,{"disambiguationData":[OSD([subQ3])]}),makeQuery(id+"F32.opExtrude","SWEPT_FACE",FACE,{"disambiguationData":[OSD([sQuery(id+"F31.wireOp",EDGE,"E36.0.5")])]})]});var subQ10=sQuery(id+"F38.wireOp",EDGE,"E38.right");Q0=makeQuery(id+"F44.opChamfer","BLEND_EDGE",EDGE,{"blendedFrom":[makeQuery(id+"F39.opExtrude","CAP_EDGE",EDGE,{"disambiguationData":[OSD([subQ10])],"isStart":false}),makeQuery(id+"F43.boolean.opBoolean","MERGE",FACE,{"derivedFrom":[makeQuery(id+"F39.boolean.opBoolean","SPLIT",FACE,{"disambiguationData":[TD([makeQuery(id+"F34.opFillet","BLEND_FACE",FACE,{"disambiguationData":[OSD([subQ7])]})])],"derivedFrom":subQ9}),makeQuery(id+"F39.boolean.opBoolean","SPLIT",FACE,{"disambiguationData":[TD([makeQuery(id+"F34.opFillet","BLEND_FACE",FACE,{"disambiguationData":[OSD([subQ0])]})])],"derivedFrom":subQ9}),makeQuery(id+"F43.opExtrude","CAP_FACE",FACE,{"disambiguationData":[OSD([sQuery(id+"F42.wireOp",EDGE,"E40.0.0"),sQuery(id+"F42.wireOp",EDGE,"E41"),sQuery(id+"F42.wireOp",EDGE,"E42"),sQuery(id+"F42.wireOp",EDGE,"E43")])],"isStart":false})]})],"blendedInto":[makeQuery(id+"F43.boolean.opBoolean","MERGE",FACE,{"derivedFrom":[makeQuery(id+"F39.boolean.opBoolean","SPLIT",FACE,{"disambiguationData":[TD([makeQuery(id+"F34.opFillet","BLEND_FACE",FACE,{"disambiguationData":[OSD([subQ7])]})])],"derivedFrom":subQ9}),makeQuery(id+"F39.boolean.opBoolean","SPLIT",FACE,{"disambiguationData":[TD([makeQuery(id+"F34.opFillet","BLEND_FACE",FACE,{"disambiguationData":[OSD([subQ0])]})])],"derivedFrom":subQ9}),makeQuery(id+"F43.opExtrude","CAP_FACE",FACE,{"disambiguationData":[OSD([sQuery(id+"F42.wireOp",EDGE,"E40.0.0"),sQuery(id+"F42.wireOp",EDGE,"E41"),sQuery(id+"F42.wireOp",EDGE,"E42"),sQuery(id+"F42.wireOp",EDGE,"E43")])],"isStart":false})]})]});}
            var Q1;
            Q1=makeQuery(id+"F43.boolean.opBoolean","COPY",EDGE,{"derivedFrom":makeQuery(id+"F43.opExtrude","CAP_EDGE",EDGE,{"disambiguationData":[OSD([sQuery(id+"F42.wireOp",EDGE,"E42")])],"isStart":false})});
            var Q2;
            {var subQ0=sQuery(id+"F31.wireOp",EDGE,"E36.0.6");var subQ3=sQuery(id+"F28.wireOp",EDGE,"E35");var subQ7=sQuery(id+"F28.wireOp",EDGE,"E29");var subQ9=sQuery(id+"F38.wireOp",EDGE,"E38.left");var subQ10=makeQuery(id+"F32.boolean.opBoolean","MERGE",FACE,{"derivedFrom":[makeQuery(id+"F29.opExtrude","SWEPT_FACE",FACE,{"disambiguationData":[OSD([subQ3])]}),makeQuery(id+"F32.opExtrude","SWEPT_FACE",FACE,{"disambiguationData":[OSD([sQuery(id+"F31.wireOp",EDGE,"E36.0.5")])]})]});Q2=makeQuery(id+"F44.opChamfer","BLEND_EDGE",EDGE,{"blendedFrom":[makeQuery(id+"F39.opExtrude","CAP_EDGE",EDGE,{"disambiguationData":[OSD([subQ9])],"isStart":false}),makeQuery(id+"F43.boolean.opBoolean","MERGE",FACE,{"derivedFrom":[makeQuery(id+"F39.boolean.opBoolean","SPLIT",FACE,{"disambiguationData":[TD([makeQuery(id+"F34.opFillet","BLEND_FACE",FACE,{"disambiguationData":[OSD([subQ7])]})])],"derivedFrom":subQ10}),makeQuery(id+"F39.boolean.opBoolean","SPLIT",FACE,{"disambiguationData":[TD([makeQuery(id+"F34.opFillet","BLEND_FACE",FACE,{"disambiguationData":[OSD([subQ0])]})])],"derivedFrom":subQ10}),makeQuery(id+"F43.opExtrude","CAP_FACE",FACE,{"disambiguationData":[OSD([sQuery(id+"F42.wireOp",EDGE,"E40.0.0"),sQuery(id+"F42.wireOp",EDGE,"E41"),sQuery(id+"F42.wireOp",EDGE,"E42"),sQuery(id+"F42.wireOp",EDGE,"E43")])],"isStart":false})]})],"blendedInto":[makeQuery(id+"F43.boolean.opBoolean","MERGE",FACE,{"derivedFrom":[makeQuery(id+"F39.boolean.opBoolean","SPLIT",FACE,{"disambiguationData":[TD([makeQuery(id+"F34.opFillet","BLEND_FACE",FACE,{"disambiguationData":[OSD([subQ7])]})])],"derivedFrom":subQ10}),makeQuery(id+"F39.boolean.opBoolean","SPLIT",FACE,{"disambiguationData":[TD([makeQuery(id+"F34.opFillet","BLEND_FACE",FACE,{"disambiguationData":[OSD([subQ0])]})])],"derivedFrom":subQ10}),makeQuery(id+"F43.opExtrude","CAP_FACE",FACE,{"disambiguationData":[OSD([sQuery(id+"F42.wireOp",EDGE,"E40.0.0"),sQuery(id+"F42.wireOp",EDGE,"E41"),sQuery(id+"F42.wireOp",EDGE,"E42"),sQuery(id+"F42.wireOp",EDGE,"E43")])],"isStart":false})]})]});}
            fillet(context, id + "F46", {"entities" : qUnion([Q0, Q1, Q2]), "radius" : 2 * mm, "tangentPropagation" : true, "allowEdgeOverflow" : false});
        }
        {
            var Q0;
            Q0=makeQuery(id+"F11.opExtrude","CAP_FACE",FACE,{"disambiguationData":[OSD([sQuery(id+"F10.wireOp",EDGE,"E16.top"),sQuery(id+"F10.wireOp",EDGE,"E16.left"),sQuery(id+"F10.wireOp",EDGE,"E16.right"),sQuery(id+"F10.wireOp",EDGE,"E18.0.0"),sQuery(id+"F10.wireOp",EDGE,"E18.0.1"),sQuery(id+"F10.wireOp",EDGE,"E18.0.2"),sQuery(id+"F10.wireOp",EDGE,"E18.0.3"),sQuery(id+"F10.wireOp",EDGE,"E18.0.4"),sQuery(id+"F10.wireOp",EDGE,"E18.0.5"),sQuery(id+"F10.wireOp",EDGE,"E18.0.6"),sQuery(id+"F10.wireOp",EDGE,"E18.0.7")])],"isStart":true});
            var sketch = newSketch(context, id + "F47", { "sketchPlane" : qUnion([Q0])});
            skCircle(sketch, "E44.0", {"center": v(3.15, 29.8) * mm, "radius": 1.75 * mm, "construction": true});
            skCircle(sketch, "E45", {"center": v(3.15, 29.8) * mm, "radius": 2.75 * mm, "construction": true});
            skLineSegment(sketch, "E46", {"start": v(5.95, 31.25) * mm, "end": v(5.84, 28.15) * mm});
            skLineSegment(sketch, "E47", {"start": v(5.84, 28.15) * mm, "end": v(3.04, 26.8) * mm});
            skLineSegment(sketch, "E48", {"start": v(3.04, 26.8) * mm, "end": v(0.41, 28.45) * mm});
            skLineSegment(sketch, "E49", {"start": v(0.41, 28.45) * mm, "end": v(0.41, 31.55) * mm});
            skLineSegment(sketch, "E50", {"start": v(0.41, 31.55) * mm, "end": v(3.26, 32.8) * mm});
            skLineSegment(sketch, "E51", {"start": v(3.26, 32.8) * mm, "end": v(5.95, 31.25) * mm});
            skSolve(sketch);
        }
        {
            var Q0;
            Q0=qSketchRegion(id+"F47",true);
            extrude(context, id + "F48", {"entities" : qUnion([Q0]), "operationType" : NewBodyOperationType.REMOVE, "oppositeDirection" : true, "depth" : 4 * mm});
        }
        {
            var Q0;
            Q0=makeQuery(id+"F14.opExtrude","CAP_FACE",FACE,{"disambiguationData":[OSD([sQuery(id+"F13.wireOp",EDGE,"E20.bottom"),sQuery(id+"F13.wireOp",EDGE,"E20.top"),sQuery(id+"F13.wireOp",EDGE,"E20.left"),sQuery(id+"F13.wireOp",EDGE,"E20.right")])],"isStart":false});
            var sketch = newSketch(context, id + "F49", { "sketchPlane" : qUnion([Q0])});
            skCircle(sketch, "E52.0", {"center": v(-41, -8.6) * mm, "radius": 1.75 * mm, "construction": true});
            skCircle(sketch, "E53", {"center": v(-41, -8.6) * mm, "radius": 2.75 * mm, "construction": true});
            skLineSegment(sketch, "E54", {"start": v(-38.25, -7.04) * mm, "end": v(-38.25, -10.15) * mm});
            skLineSegment(sketch, "E55", {"start": v(-38.25, -10.15) * mm, "end": v(-41, -11.6) * mm});
            skLineSegment(sketch, "E56", {"start": v(-41, -11.6) * mm, "end": v(-43.75, -10.16) * mm});
            skLineSegment(sketch, "E57", {"start": v(-43.75, -10.16) * mm, "end": v(-43.75, -7.06) * mm});
            skLineSegment(sketch, "E58", {"start": v(-43.75, -7.06) * mm, "end": v(-41, -5.6) * mm});
            skLineSegment(sketch, "E59", {"start": v(-41, -5.6) * mm, "end": v(-38.25, -7.04) * mm});
            skSolve(sketch);
        }
        {
            var Q0;
            Q0=qSketchRegion(id+"F49",true);
            extrude(context, id + "F50", {"entities" : qUnion([Q0]), "operationType" : NewBodyOperationType.REMOVE, "oppositeDirection" : true, "depth" : 4 * mm});
        }
    });
